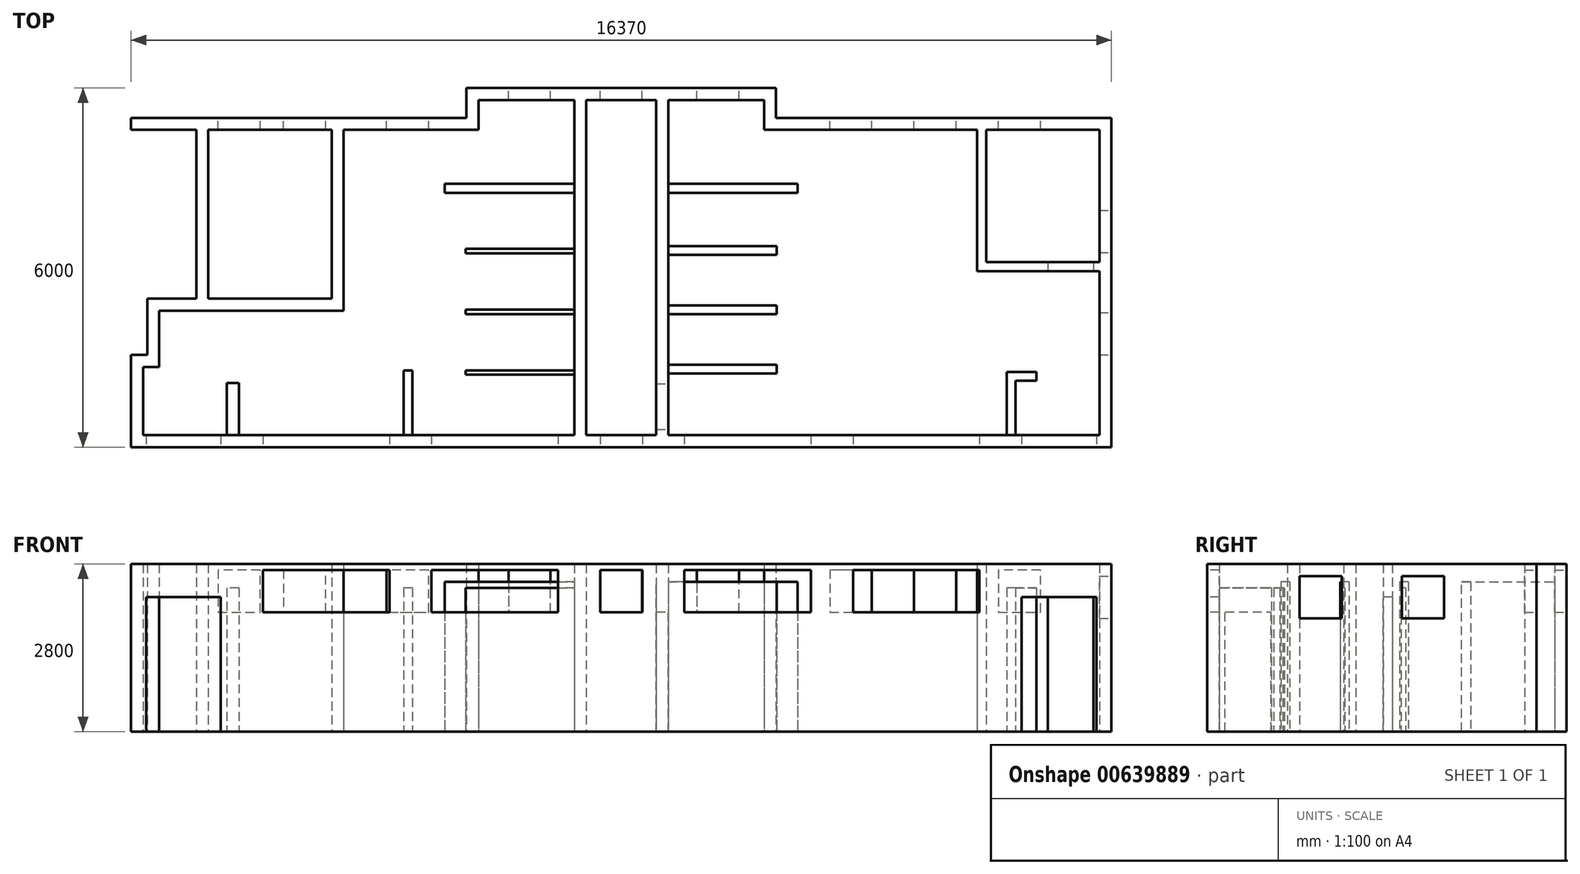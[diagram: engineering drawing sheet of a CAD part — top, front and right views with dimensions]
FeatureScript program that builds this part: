
annotation { "Feature Type Name" : "Feature", "Feature Type Description" : "" }
export const myFeature = defineFeature(function(context is Context, id is Id, definition is map)
    precondition{}
    {
        {
            var Q0;
            Q0=qCreatedBy(makeId("Top.planeOp"),FACE);
            var sketch = newSketch(context, id + "F0", { "sketchPlane" : qUnion([Q0])});
            skLineSegment(sketch, "E0", {"start": v(5800, 5300) * mm, "end": v(5800, 5800) * mm});
            skLineSegment(sketch, "E1", {"start": v(0, 0) * mm, "end": v(16370, 0) * mm});
            skLineSegment(sketch, "E2", {"start": v(16370, 0) * mm, "end": v(16370, 5500) * mm});
            skLineSegment(sketch, "E3", {"start": v(16370, 5500) * mm, "end": v(10770, 5500) * mm});
            skLineSegment(sketch, "E4", {"start": v(10770, 5500) * mm, "end": v(10770, 6000) * mm});
            skLineSegment(sketch, "E5", {"start": v(10770, 6000) * mm, "end": v(5600, 6000) * mm});
            skLineSegment(sketch, "E6", {"start": v(5600, 6000) * mm, "end": v(5600, 5500) * mm});
            skLineSegment(sketch, "E7", {"start": v(10570, 5800) * mm, "end": v(10570, 5300) * mm});
            skLineSegment(sketch, "E8", {"start": v(10570, 5300) * mm, "end": v(16170, 5300) * mm});
            skLineSegment(sketch, "E9", {"start": v(16170, 5300) * mm, "end": v(16170, 200) * mm});
            skLineSegment(sketch, "E10", {"start": v(0, 200) * mm, "end": v(0, 0) * mm});
            skLineSegment(sketch, "E11", {"start": v(0, 0) * mm, "end": v(0, 1540) * mm});
            skPoint(sketch, "E11.endSnap0", {"position": v(0, 100) * mm});
            skLineSegment(sketch, "E12", {"start": v(16170, 200) * mm, "end": v(200, 200) * mm});
            skLineSegment(sketch, "E13", {"start": v(200, 200) * mm, "end": v(200, 1340) * mm});
            skLineSegment(sketch, "E14", {"start": v(200, 1340) * mm, "end": v(470, 1340) * mm});
            skLineSegment(sketch, "E15", {"start": v(0, 1540) * mm, "end": v(270, 1540) * mm});
            skLineSegment(sketch, "E16", {"start": v(270, 1540) * mm, "end": v(270, 2480) * mm});
            skLineSegment(sketch, "E17", {"start": v(470, 1340) * mm, "end": v(470, 2280) * mm});
            skLineSegment(sketch, "E18", {"start": v(470, 2280) * mm, "end": v(936.4, 2280) * mm});
            skLineSegment(sketch, "E19", {"start": v(270, 2480) * mm, "end": v(1090, 2480) * mm});
            skLineSegment(sketch, "E20", {"start": v(5600, 5500) * mm, "end": v(1090, 5500) * mm});
            skLineSegment(sketch, "E21", {"start": v(5800, 5300) * mm, "end": v(1290, 5300) * mm});
            skLineSegment(sketch, "E22", {"start": v(1290, 5300) * mm, "end": v(1290, 2280) * mm});
            skLineSegment(sketch, "E23", {"start": v(1290, 2280) * mm, "end": v(936.4, 2280) * mm});
            skLineSegment(sketch, "E24", {"start": v(1090, 2480) * mm, "end": v(1090, 5500) * mm});
            skLineSegment(sketch, "E25", {"start": v(10570, 5800) * mm, "end": v(5800, 5800) * mm});
            skLineSegment(sketch, "E26", {"start": v(1090, 5500) * mm, "end": v(1090, 5300) * mm});
            skLineSegment(sketch, "E27", {"start": v(1090, 5500) * mm, "end": v(0, 5500) * mm});
            skLineSegment(sketch, "E28", {"start": v(0, 5500) * mm, "end": v(0, 5042) * mm});
            skLineSegment(sketch, "E29", {"start": v(0, 5042) * mm, "end": v(458, 5042) * mm});
            skLineSegment(sketch, "E30", {"start": v(458, 5042) * mm, "end": v(458, 5300) * mm});
            skLineSegment(sketch, "E31", {"start": v(458, 5300) * mm, "end": v(1090, 5300) * mm});
            skSolve(sketch);
        }
        {
            var Q0;
            {var subQ2=sQuery(id+"F0.wireOp",EDGE,"E1");Q0=makeQuery(id+"F0.imprint","IMPRINT",FACE,{"disambiguationData":[TD([[makeQuery(id+"F0.imprint","IMPRINT",EDGE,{"derivedFrom":subQ2}),1.0]])]});}
            extrude(context, id + "F1", {"entities" : qUnion([Q0]), "depth" : 2800 * mm, "offsetDistance" : 25 * mm});
        }
        {
            var Q0;
            Q0=makeQuery(id+"F1.opExtrude","SWEPT_FACE",FACE,{"disambiguationData":[OSD([sQuery(id+"F0.wireOp",EDGE,"E1")])]});
            var sketch = newSketch(context, id + "F2", { "sketchPlane" : qUnion([Q0])});
            skLineSegment(sketch, "E32", {"start": v(250, 0) * mm, "end": v(250, 2250) * mm});
            skLineSegment(sketch, "E33", {"start": v(250, 2250) * mm, "end": v(1500, 2250) * mm});
            skLineSegment(sketch, "E34", {"start": v(1500, 2250) * mm, "end": v(1500, 0) * mm});
            skLineSegment(sketch, "E35", {"start": v(1500, 0) * mm, "end": v(250, 0) * mm});
            skSolve(sketch);
        }
        {
            var Q0;
            Q0=makeQuery(id+"F2.imprint","IMPRINT",FACE,{"disambiguationData":[TD([[makeQuery(id+"F2.imprint","IMPRINT",EDGE,{"derivedFrom":sQuery(id+"F2.wireOp",EDGE,"E32")}),-1.0]])]});
            extrude(context, id + "F3", {"entities" : qUnion([Q0]), "operationType" : NewBodyOperationType.REMOVE, "oppositeDirection" : true, "depth" : 200 * mm, "offsetDistance" : 25 * mm});
        }
        {
            var Q0;
            Q0=makeQuery(id+"F1.opExtrude","SWEPT_FACE",FACE,{"disambiguationData":[OSD([sQuery(id+"F0.wireOp",EDGE,"E1")])]});
            var sketch = newSketch(context, id + "F4", { "sketchPlane" : qUnion([Q0])});
            skLineSegment(sketch, "E36", {"start": v(16120, 0) * mm, "end": v(16120, 2250) * mm});
            skLineSegment(sketch, "E37", {"start": v(16120, 2250) * mm, "end": v(14870, 2250) * mm});
            skLineSegment(sketch, "E38", {"start": v(14870, 2250) * mm, "end": v(14870, 0) * mm});
            skLineSegment(sketch, "E39", {"start": v(14870, 0) * mm, "end": v(16120, 0) * mm});
            skSolve(sketch);
        }
        {
            var Q0;
            Q0=makeQuery(id+"F4.imprint","IMPRINT",FACE,{"disambiguationData":[TD([[makeQuery(id+"F4.imprint","IMPRINT",EDGE,{"derivedFrom":sQuery(id+"F4.wireOp",EDGE,"E36")}),1.0]])]});
            extrude(context, id + "F5", {"entities" : qUnion([Q0]), "operationType" : NewBodyOperationType.REMOVE, "oppositeDirection" : true, "depth" : 200 * mm, "offsetDistance" : 25 * mm});
        }
        {
            var Q0;
            Q0=qCreatedBy(makeId("Top.planeOp"),FACE);
            var sketch = newSketch(context, id + "F6", { "sketchPlane" : qUnion([Q0])});
            skLineSegment(sketch, "E40", {"start": v(1290, 2280) * mm, "end": v(3550, 2280) * mm});
            skLineSegment(sketch, "E41", {"start": v(3550, 2280) * mm, "end": v(3550, 5300) * mm});
            skLineSegment(sketch, "E42", {"start": v(3550, 5300) * mm, "end": v(3350, 5300) * mm});
            skLineSegment(sketch, "E43", {"start": v(3350, 2480) * mm, "end": v(1290, 2480) * mm});
            skLineSegment(sketch, "E44", {"start": v(1290, 2480) * mm, "end": v(1290, 2280) * mm});
            skLineSegment(sketch, "E45", {"start": v(3350, 5300) * mm, "end": v(3350, 2480) * mm});
            skSolve(sketch);
        }
        {
            var Q0;
            Q0=makeQuery(id+"F6.imprint","IMPRINT",FACE,{"disambiguationData":[TD([[makeQuery(id+"F6.imprint","IMPRINT",EDGE,{"derivedFrom":sQuery(id+"F6.wireOp",EDGE,"E40")}),1.0]])]});
            extrude(context, id + "F7", {"entities" : qUnion([Q0]), "operationType" : NewBodyOperationType.ADD, "depth" : 2800 * mm, "offsetDistance" : 25 * mm});
        }
        {
            var Q0;
            Q0=qCreatedBy(makeId("Top.planeOp"),FACE);
            var sketch = newSketch(context, id + "F8", { "sketchPlane" : qUnion([Q0])});
            skLineSegment(sketch, "E46.0", {"start": v(5800, 5300) * mm, "end": v(5800, 5800) * mm});
            skLineSegment(sketch, "E47.0", {"start": v(10570, 5800) * mm, "end": v(5800, 5800) * mm});
            skLineSegment(sketch, "E48.0", {"start": v(16170, 200) * mm, "end": v(200, 200) * mm});
            skLineSegment(sketch, "E49", {"start": v(5800, 5800) * mm, "end": v(7400, 5800) * mm});
            skLineSegment(sketch, "E50", {"start": v(7400, 5800) * mm, "end": v(7600, 5800) * mm});
            skLineSegment(sketch, "E51", {"start": v(7600, 5800) * mm, "end": v(7600, 200) * mm});
            skLineSegment(sketch, "E52", {"start": v(7400, 5800) * mm, "end": v(7400, 200) * mm});
            skSolve(sketch);
        }
        {
            var Q0;
            Q0=qCreatedBy(makeId("Top.planeOp"),FACE);
            var sketch = newSketch(context, id + "F9", { "sketchPlane" : qUnion([Q0])});
            skLineSegment(sketch, "E53.0", {"start": v(10570, 5800) * mm, "end": v(10570, 5300) * mm});
            skLineSegment(sketch, "E53.1", {"start": v(10570, 5800) * mm, "end": v(5800, 5800) * mm});
            skLineSegment(sketch, "E53.2", {"start": v(16170, 200) * mm, "end": v(200, 200) * mm});
            skLineSegment(sketch, "E54", {"start": v(8970, 200) * mm, "end": v(8770, 200) * mm});
            skLineSegment(sketch, "E55", {"start": v(8770, 200) * mm, "end": v(8770, 5800) * mm});
            skLineSegment(sketch, "E56", {"start": v(8770, 5800) * mm, "end": v(8970, 5800) * mm});
            skLineSegment(sketch, "E57", {"start": v(8970, 5800) * mm, "end": v(8970, 200) * mm});
            skSolve(sketch);
        }
        {
            var Q0;
            Q0=qSketchRegion(id+"F8",true);
            extrude(context, id + "F10", {"entities" : qUnion([Q0]), "operationType" : NewBodyOperationType.ADD, "depth" : 2800 * mm, "offsetDistance" : 25 * mm});
        }
        {
            var Q0;
            Q0=qSketchRegion(id+"F9",true);
            extrude(context, id + "F11", {"entities" : qUnion([Q0]), "operationType" : NewBodyOperationType.ADD, "depth" : 2800 * mm, "offsetDistance" : 25 * mm});
        }
        {
            var Q0;
            Q0=qCreatedBy(makeId("Top.planeOp"),FACE);
            var sketch = newSketch(context, id + "F12", { "sketchPlane" : qUnion([Q0])});
            skLineSegment(sketch, "E58.0", {"start": v(10570, 5800) * mm, "end": v(5800, 5800) * mm});
            skLineSegment(sketch, "E58.1", {"start": v(10570, 5800) * mm, "end": v(10570, 5300) * mm});
            skLineSegment(sketch, "E59", {"start": v(10570, 5800) * mm, "end": v(8969, 5800) * mm});
            skLineSegment(sketch, "E60", {"start": v(8969, 5800) * mm, "end": v(8969, 4400) * mm});
            skLineSegment(sketch, "E61", {"start": v(8969, 4400) * mm, "end": v(11129, 4400) * mm});
            skLineSegment(sketch, "E62", {"start": v(11129, 4400) * mm, "end": v(11129, 4250) * mm});
            skLineSegment(sketch, "E63", {"start": v(11129, 4250) * mm, "end": v(8769, 4250) * mm});
            skLineSegment(sketch, "E64", {"start": v(8769, 4250) * mm, "end": v(8769, 5800) * mm});
            skSolve(sketch);
        }
        {
            var Q0;
            Q0=qCreatedBy(makeId("Top.planeOp"),FACE);
            var sketch = newSketch(context, id + "F13", { "sketchPlane" : qUnion([Q0])});
            skLineSegment(sketch, "E65", {"start": v(7400, 5800) * mm, "end": v(7400, 4400) * mm});
            skLineSegment(sketch, "E66", {"start": v(7400, 4400) * mm, "end": v(5240, 4400) * mm});
            skLineSegment(sketch, "E67", {"start": v(5240, 4400) * mm, "end": v(5240, 4250) * mm});
            skLineSegment(sketch, "E68", {"start": v(5240, 4250) * mm, "end": v(7600, 4250) * mm});
            skLineSegment(sketch, "E69", {"start": v(7600, 4250) * mm, "end": v(7600, 5800) * mm});
            skLineSegment(sketch, "E70", {"start": v(7400, 5800) * mm, "end": v(7600, 5800) * mm});
            skSolve(sketch);
        }
        {
            var Q0;
            Q0=qSketchRegion(id+"F13",true);
            extrude(context, id + "F14", {"entities" : qUnion([Q0]), "operationType" : NewBodyOperationType.ADD, "depth" : 2500 * mm, "offsetDistance" : 25 * mm});
        }
        {
            var Q0;
            Q0=qCreatedBy(makeId("Top.planeOp"),FACE);
            var sketch = newSketch(context, id + "F15", { "sketchPlane" : qUnion([Q0])});
            skLineSegment(sketch, "E71.0", {"start": v(10570, 5300) * mm, "end": v(16170, 5300) * mm});
            skLineSegment(sketch, "E71.1", {"start": v(16170, 5300) * mm, "end": v(16170, 200) * mm});
            skLineSegment(sketch, "E72", {"start": v(16170, 5300) * mm, "end": v(16170, 3090) * mm});
            skLineSegment(sketch, "E73", {"start": v(16170, 3090) * mm, "end": v(14280, 3090) * mm});
            skLineSegment(sketch, "E74", {"start": v(14280, 3090) * mm, "end": v(14280, 5300) * mm});
            skLineSegment(sketch, "E75", {"start": v(14280, 5300) * mm, "end": v(14130, 5300) * mm});
            skLineSegment(sketch, "E76", {"start": v(14130, 5300) * mm, "end": v(14130, 2940) * mm});
            skLineSegment(sketch, "E77", {"start": v(14130, 2940) * mm, "end": v(16170, 2940) * mm});
            skSolve(sketch);
        }
        {
            var Q0;
            {var subQ0=sQuery(id+"F15.wireOp",EDGE,"E73");Q0=makeQuery(id+"F15.imprint","IMPRINT",FACE,{"disambiguationData":[TD([[makeQuery(id+"F15.imprint","IMPRINT",EDGE,{"derivedFrom":subQ0}),1.0]])]});}
            extrude(context, id + "F16", {"entities" : qUnion([Q0]), "operationType" : NewBodyOperationType.ADD, "depth" : 2800 * mm, "offsetDistance" : 25 * mm});
        }
        {
            var Q0;
            Q0=makeQuery(id+"F1.opExtrude","SWEPT_FACE",FACE,{"disambiguationData":[OSD([sQuery(id+"F0.wireOp",EDGE,"E1")])]});
            var sketch = newSketch(context, id + "F17", { "sketchPlane" : qUnion([Q0])});
            skLineSegment(sketch, "E78", {"start": v(2204, 1996) * mm, "end": v(2204, 2700) * mm});
            skLineSegment(sketch, "E79", {"start": v(2204, 2700) * mm, "end": v(4315, 2700) * mm});
            skLineSegment(sketch, "E80", {"start": v(4315, 2700) * mm, "end": v(4315, 1996) * mm});
            skLineSegment(sketch, "E81", {"start": v(4315, 1996) * mm, "end": v(2204, 1996) * mm});
            skLineSegment(sketch, "E82", {"start": v(5018, 1996) * mm, "end": v(5018, 2700) * mm});
            skLineSegment(sketch, "E83", {"start": v(5018, 2700) * mm, "end": v(7129, 2700) * mm});
            skLineSegment(sketch, "E84", {"start": v(7129, 2700) * mm, "end": v(7129, 1996) * mm});
            skLineSegment(sketch, "E85", {"start": v(7129, 1996) * mm, "end": v(5018, 1996) * mm});
            skLineSegment(sketch, "E86", {"start": v(7833, 1996) * mm, "end": v(7833, 2700) * mm});
            skLineSegment(sketch, "E87", {"start": v(7833, 2700) * mm, "end": v(8537, 2700) * mm});
            skLineSegment(sketch, "E88", {"start": v(8537, 2700) * mm, "end": v(8537, 1996) * mm});
            skLineSegment(sketch, "E89", {"start": v(8537, 1996) * mm, "end": v(7833, 1996) * mm});
            skLineSegment(sketch, "E90", {"start": v(9241, 1996) * mm, "end": v(9241, 2700) * mm});
            skLineSegment(sketch, "E91", {"start": v(9241, 2700) * mm, "end": v(11352, 2700) * mm});
            skLineSegment(sketch, "E92", {"start": v(11352, 2700) * mm, "end": v(11352, 1996) * mm});
            skLineSegment(sketch, "E93", {"start": v(11352, 1996) * mm, "end": v(9241, 1996) * mm});
            skLineSegment(sketch, "E94", {"start": v(12056, 1996) * mm, "end": v(12056, 2700) * mm});
            skLineSegment(sketch, "E95", {"start": v(12056, 2700) * mm, "end": v(14167, 2700) * mm});
            skLineSegment(sketch, "E96", {"start": v(14167, 2700) * mm, "end": v(14167, 1996) * mm});
            skLineSegment(sketch, "E97", {"start": v(14167, 1996) * mm, "end": v(12056, 1996) * mm});
            skSolve(sketch);
        }
        {
            var Q0;
            Q0=makeQuery(id+"F17.imprint","IMPRINT",FACE,{"disambiguationData":[TD([[makeQuery(id+"F17.imprint","IMPRINT",EDGE,{"derivedFrom":sQuery(id+"F17.wireOp",EDGE,"E78")}),-1.0]])]});
            var Q1;
            Q1=makeQuery(id+"F17.imprint","IMPRINT",FACE,{"disambiguationData":[TD([[makeQuery(id+"F17.imprint","IMPRINT",EDGE,{"derivedFrom":sQuery(id+"F17.wireOp",EDGE,"E82")}),-1.0]])]});
            var Q2;
            Q2=makeQuery(id+"F17.imprint","IMPRINT",FACE,{"disambiguationData":[TD([[makeQuery(id+"F17.imprint","IMPRINT",EDGE,{"derivedFrom":sQuery(id+"F17.wireOp",EDGE,"E86")}),-1.0]])]});
            var Q3;
            Q3=makeQuery(id+"F17.imprint","IMPRINT",FACE,{"disambiguationData":[TD([[makeQuery(id+"F17.imprint","IMPRINT",EDGE,{"derivedFrom":sQuery(id+"F17.wireOp",EDGE,"E90")}),-1.0]])]});
            var Q4;
            Q4=makeQuery(id+"F17.imprint","IMPRINT",FACE,{"disambiguationData":[TD([[makeQuery(id+"F17.imprint","IMPRINT",EDGE,{"derivedFrom":sQuery(id+"F17.wireOp",EDGE,"E94")}),-1.0]])]});
            extrude(context, id + "F18", {"entities" : qUnion([Q0, Q1, Q2, Q3, Q4]), "operationType" : NewBodyOperationType.REMOVE, "oppositeDirection" : true, "depth" : 200 * mm, "offsetDistance" : 25 * mm});
        }
        {
            var Q0;
            {var subQ0=sQuery(id+"F12.wireOp",EDGE,"E60");Q0=makeQuery(id+"F12.imprint","IMPRINT",FACE,{"disambiguationData":[TD([[makeQuery(id+"F12.imprint","IMPRINT",EDGE,{"derivedFrom":subQ0}),-1.0]])]});}
            extrude(context, id + "F19", {"entities" : qUnion([Q0]), "operationType" : NewBodyOperationType.ADD, "depth" : 2500 * mm, "offsetDistance" : 25 * mm});
        }
        {
            var Q0;
            Q0=makeQuery(id+"F1.opExtrude","SWEPT_FACE",FACE,{"disambiguationData":[OSD([sQuery(id+"F0.wireOp",EDGE,"E3")])]});
            var sketch = newSketch(context, id + "F20", { "sketchPlane" : qUnion([Q0])});
            skLineSegment(sketch, "E98", {"start": v(-15187, 1996) * mm, "end": v(-15187, 2700) * mm});
            skLineSegment(sketch, "E99", {"start": v(-15187, 2700) * mm, "end": v(-14483, 2700) * mm});
            skLineSegment(sketch, "E100", {"start": v(-14483, 2700) * mm, "end": v(-14483, 1996) * mm});
            skLineSegment(sketch, "E101", {"start": v(-14483, 1996) * mm, "end": v(-15187, 1996) * mm});
            skLineSegment(sketch, "E102", {"start": v(-13779, 1996) * mm, "end": v(-13779, 2700) * mm});
            skLineSegment(sketch, "E103", {"start": v(-13779, 2700) * mm, "end": v(-13075, 2700) * mm});
            skLineSegment(sketch, "E104", {"start": v(-13075, 2700) * mm, "end": v(-13075, 1996) * mm});
            skLineSegment(sketch, "E105", {"start": v(-13075, 1996) * mm, "end": v(-13779, 1996) * mm});
            skLineSegment(sketch, "E106", {"start": v(-12371, 1996) * mm, "end": v(-12371, 2700) * mm});
            skLineSegment(sketch, "E107", {"start": v(-12371, 2700) * mm, "end": v(-11667, 2700) * mm});
            skLineSegment(sketch, "E108", {"start": v(-11667, 2700) * mm, "end": v(-11667, 1996) * mm});
            skLineSegment(sketch, "E109", {"start": v(-11667, 1996) * mm, "end": v(-12371, 1996) * mm});
            skSolve(sketch);
        }
        {
            var Q0;
            Q0=makeQuery(id+"F20.imprint","IMPRINT",FACE,{"disambiguationData":[TD([[makeQuery(id+"F20.imprint","IMPRINT",EDGE,{"derivedFrom":sQuery(id+"F20.wireOp",EDGE,"E98")}),-1.0]])]});
            var Q1;
            Q1=makeQuery(id+"F20.imprint","IMPRINT",FACE,{"disambiguationData":[TD([[makeQuery(id+"F20.imprint","IMPRINT",EDGE,{"derivedFrom":sQuery(id+"F20.wireOp",EDGE,"E102")}),-1.0]])]});
            var Q2;
            Q2=makeQuery(id+"F20.imprint","IMPRINT",FACE,{"disambiguationData":[TD([[makeQuery(id+"F20.imprint","IMPRINT",EDGE,{"derivedFrom":sQuery(id+"F20.wireOp",EDGE,"E106")}),-1.0]])]});
            extrude(context, id + "F21", {"entities" : qUnion([Q0, Q1, Q2]), "operationType" : NewBodyOperationType.REMOVE, "oppositeDirection" : true, "depth" : 200 * mm, "offsetDistance" : 25 * mm});
        }
        {
            var Q0;
            Q0=makeQuery(id+"F1.opExtrude","SWEPT_FACE",FACE,{"disambiguationData":[OSD([sQuery(id+"F0.wireOp",EDGE,"E5")])]});
            var sketch = newSketch(context, id + "F22", { "sketchPlane" : qUnion([Q0])});
            skLineSegment(sketch, "E110", {"start": v(-10150, 1996) * mm, "end": v(-10150, 2700) * mm});
            skLineSegment(sketch, "E111", {"start": v(-10150, 2700) * mm, "end": v(-9446, 2700) * mm});
            skLineSegment(sketch, "E112", {"start": v(-9446, 2700) * mm, "end": v(-9446, 1996) * mm});
            skLineSegment(sketch, "E113", {"start": v(-9446, 1996) * mm, "end": v(-10150, 1996) * mm});
            skLineSegment(sketch, "E114", {"start": v(-8536, 1996) * mm, "end": v(-8536, 2700) * mm});
            skLineSegment(sketch, "E115", {"start": v(-8536, 2700) * mm, "end": v(-7832, 2700) * mm});
            skLineSegment(sketch, "E116", {"start": v(-7832, 2700) * mm, "end": v(-7832, 1996) * mm});
            skLineSegment(sketch, "E117", {"start": v(-7832, 1996) * mm, "end": v(-8536, 1996) * mm});
            skLineSegment(sketch, "E118", {"start": v(-7005, 1996) * mm, "end": v(-7005, 2700) * mm});
            skLineSegment(sketch, "E119", {"start": v(-7005, 2700) * mm, "end": v(-6301, 2700) * mm});
            skLineSegment(sketch, "E120", {"start": v(-6301, 2700) * mm, "end": v(-6301, 1996) * mm});
            skLineSegment(sketch, "E121", {"start": v(-6301, 1996) * mm, "end": v(-7005, 1996) * mm});
            skSolve(sketch);
        }
        {
            var Q0;
            Q0=makeQuery(id+"F22.imprint","IMPRINT",FACE,{"disambiguationData":[TD([[makeQuery(id+"F22.imprint","IMPRINT",EDGE,{"derivedFrom":sQuery(id+"F22.wireOp",EDGE,"E110")}),-1.0]])]});
            var Q1;
            Q1=makeQuery(id+"F22.imprint","IMPRINT",FACE,{"disambiguationData":[TD([[makeQuery(id+"F22.imprint","IMPRINT",EDGE,{"derivedFrom":sQuery(id+"F22.wireOp",EDGE,"E114")}),-1.0]])]});
            var Q2;
            Q2=makeQuery(id+"F22.imprint","IMPRINT",FACE,{"disambiguationData":[TD([[makeQuery(id+"F22.imprint","IMPRINT",EDGE,{"derivedFrom":sQuery(id+"F22.wireOp",EDGE,"E118")}),-1.0]])]});
            extrude(context, id + "F23", {"entities" : qUnion([Q0, Q1, Q2]), "operationType" : NewBodyOperationType.REMOVE, "oppositeDirection" : true, "depth" : 200 * mm, "offsetDistance" : 25 * mm});
        }
        {
            var Q0;
            Q0=makeQuery(id+"F1.opExtrude","SWEPT_FACE",FACE,{"disambiguationData":[OSD([sQuery(id+"F0.wireOp",EDGE,"E20")])]});
            var sketch = newSketch(context, id + "F24", { "sketchPlane" : qUnion([Q0])});
            skLineSegment(sketch, "E122", {"start": v(-4969, 1996) * mm, "end": v(-4969, 2700) * mm});
            skLineSegment(sketch, "E123", {"start": v(-4969, 2700) * mm, "end": v(-4265, 2700) * mm});
            skLineSegment(sketch, "E124", {"start": v(-4265, 2700) * mm, "end": v(-4265, 1996) * mm});
            skLineSegment(sketch, "E125", {"start": v(-4265, 1996) * mm, "end": v(-4969, 1996) * mm});
            skLineSegment(sketch, "E126", {"start": v(-3248, 1996) * mm, "end": v(-3248, 2700) * mm});
            skLineSegment(sketch, "E127", {"start": v(-3248, 2700) * mm, "end": v(-2544, 2700) * mm});
            skLineSegment(sketch, "E128", {"start": v(-2544, 2700) * mm, "end": v(-2544, 1996) * mm});
            skLineSegment(sketch, "E129", {"start": v(-2544, 1996) * mm, "end": v(-3248, 1996) * mm});
            skLineSegment(sketch, "E130", {"start": v(-2156, 1996) * mm, "end": v(-2156, 2700) * mm});
            skLineSegment(sketch, "E131", {"start": v(-2156, 2700) * mm, "end": v(-1452, 2700) * mm});
            skLineSegment(sketch, "E132", {"start": v(-1452, 2700) * mm, "end": v(-1452, 1996) * mm});
            skLineSegment(sketch, "E133", {"start": v(-1452, 1996) * mm, "end": v(-2156, 1996) * mm});
            skSolve(sketch);
        }
        {
            var Q0;
            Q0=makeQuery(id+"F24.imprint","IMPRINT",FACE,{"disambiguationData":[TD([[makeQuery(id+"F24.imprint","IMPRINT",EDGE,{"derivedFrom":sQuery(id+"F24.wireOp",EDGE,"E122")}),-1.0]])]});
            var Q1;
            Q1=makeQuery(id+"F24.imprint","IMPRINT",FACE,{"disambiguationData":[TD([[makeQuery(id+"F24.imprint","IMPRINT",EDGE,{"derivedFrom":sQuery(id+"F24.wireOp",EDGE,"E126")}),-1.0]])]});
            var Q2;
            Q2=makeQuery(id+"F24.imprint","IMPRINT",FACE,{"disambiguationData":[TD([[makeQuery(id+"F24.imprint","IMPRINT",EDGE,{"derivedFrom":sQuery(id+"F24.wireOp",EDGE,"E130")}),-1.0]])]});
            extrude(context, id + "F25", {"entities" : qUnion([Q0, Q1, Q2]), "operationType" : NewBodyOperationType.REMOVE, "oppositeDirection" : true, "depth" : 200 * mm, "offsetDistance" : 25 * mm});
        }
        {
            var Q0;
            Q0=makeQuery(id+"F10.opExtrude","SWEPT_FACE",FACE,{"disambiguationData":[OSD([sQuery(id+"F8.wireOp",EDGE,"E51")])]});
            var sketch = newSketch(context, id + "F26", { "sketchPlane" : qUnion([Q0])});
            skLineSegment(sketch, "E134.0", {"start": v(5800, 2800) * mm, "end": v(5800, 0) * mm});
            skLineSegment(sketch, "E135.0", {"start": v(4250, 0) * mm, "end": v(5800, 0) * mm});
            skLineSegment(sketch, "E136", {"start": v(5800, 0) * mm, "end": v(2800, 0) * mm});
            skLineSegment(sketch, "E137", {"start": v(2800, 0) * mm, "end": v(2800, 2100) * mm});
            skLineSegment(sketch, "E138", {"start": v(2800, 2100) * mm, "end": v(1200, 2100) * mm});
            skLineSegment(sketch, "E139", {"start": v(1200, 2100) * mm, "end": v(1200, 0) * mm});
            skLineSegment(sketch, "E140", {"start": v(1200, 0) * mm, "end": v(2800, 0) * mm});
            skSolve(sketch);
        }
        {
            var Q0;
            {var subQ0=sQuery(id+"F13.wireOp",EDGE,"E66");Q0=makeQuery(id+"FqNkP1vWDE5f3xF_1.boolean.opBoolean","MERGE",FACE,{"derivedFrom":[makeQuery(id+"F14.opExtrude","SWEPT_FACE",FACE,{"disambiguationData":[OSD([subQ0])]}),makeQuery(id+"FqNkP1vWDE5f3xF_1.opExtrude","SWEPT_FACE",FACE,{"disambiguationData":[OSD([subQ0])]})]});}
            var sketch = newSketch(context, id + "F27", { "sketchPlane" : qUnion([Q0])});
            skLineSegment(sketch, "E141", {"start": v(-5240, 2800) * mm, "end": v(-5240, 2450) * mm});
            skLineSegment(sketch, "E142", {"start": v(-5240, 2450) * mm, "end": v(-5390, 2450) * mm});
            skLineSegment(sketch, "E143", {"start": v(-5390, 2450) * mm, "end": v(-5390, 2800) * mm});
            skLineSegment(sketch, "E144", {"start": v(-5390, 2800) * mm, "end": v(-5240, 2800) * mm});
            skSolve(sketch);
        }
        {
            var Q0;
            Q0=makeQuery(id+"F16.opExtrude","SWEPT_FACE",FACE,{"disambiguationData":[OSD([sQuery(id+"F15.wireOp",EDGE,"E77")])]});
            var sketch = newSketch(context, id + "F28", { "sketchPlane" : qUnion([Q0])});
            skLineSegment(sketch, "E145.0", {"start": v(16170, 2800) * mm, "end": v(16170, 0) * mm});
            skLineSegment(sketch, "E146", {"start": v(16170, 0) * mm, "end": v(16070, 0) * mm});
            skLineSegment(sketch, "E147", {"start": v(16070, 0) * mm, "end": v(16070, 2250) * mm});
            skLineSegment(sketch, "E148", {"start": v(16070, 2250) * mm, "end": v(15310, 2250) * mm});
            skLineSegment(sketch, "E149", {"start": v(15310, 2250) * mm, "end": v(15310, 0) * mm});
            skLineSegment(sketch, "E150", {"start": v(15310, 0) * mm, "end": v(16070, 0) * mm});
            skSolve(sketch);
        }
        {
            var Q0;
            Q0=qSketchRegion(id+"F28",true);
            extrude(context, id + "F29", {"entities" : qUnion([Q0]), "operationType" : NewBodyOperationType.REMOVE, "oppositeDirection" : true, "depth" : 150 * mm, "offsetDistance" : 25 * mm});
        }
        {
            var Q0;
            Q0=makeQuery(id+"F1.opExtrude","SWEPT_FACE",FACE,{"disambiguationData":[OSD([sQuery(id+"F0.wireOp",EDGE,"E2")])]});
            var sketch = newSketch(context, id + "F30", { "sketchPlane" : qUnion([Q0])});
            skLineSegment(sketch, "E151.0", {"start": v(0, 2800) * mm, "end": v(0, 0) * mm});
            skLineSegment(sketch, "E152", {"start": v(1545, 2600) * mm, "end": v(1545, 1895) * mm});
            skLineSegment(sketch, "E153", {"start": v(1545, 1895) * mm, "end": v(2250, 1895) * mm});
            skLineSegment(sketch, "E154", {"start": v(2250, 1895) * mm, "end": v(2250, 2600) * mm});
            skLineSegment(sketch, "E155", {"start": v(2250, 2600) * mm, "end": v(1545, 2600) * mm});
            skLineSegment(sketch, "E156", {"start": v(3250, 2600) * mm, "end": v(3250, 1895) * mm});
            skLineSegment(sketch, "E157", {"start": v(3250, 1895) * mm, "end": v(3955, 1895) * mm});
            skLineSegment(sketch, "E158", {"start": v(3955, 1895) * mm, "end": v(3955, 2600) * mm});
            skLineSegment(sketch, "E159", {"start": v(3955, 2600) * mm, "end": v(3250, 2600) * mm});
            skSolve(sketch);
        }
        {
            var Q0;
            Q0=makeQuery(id+"F30.imprint","IMPRINT",FACE,{"disambiguationData":[TD([[makeQuery(id+"F30.imprint","IMPRINT",EDGE,{"derivedFrom":sQuery(id+"F30.wireOp",EDGE,"E152")}),1.0]])]});
            var Q1;
            Q1=makeQuery(id+"F30.imprint","IMPRINT",FACE,{"disambiguationData":[TD([[makeQuery(id+"F30.imprint","IMPRINT",EDGE,{"derivedFrom":sQuery(id+"F30.wireOp",EDGE,"E156")}),1.0]])]});
            extrude(context, id + "F31", {"entities" : qUnion([Q0, Q1]), "operationType" : NewBodyOperationType.REMOVE, "oppositeDirection" : true, "depth" : 200 * mm, "offsetDistance" : 25 * mm});
        }
        {
            var Q0;
            Q0=qCreatedBy(makeId("Top.planeOp"),FACE);
            var sketch = newSketch(context, id + "F32", { "sketchPlane" : qUnion([Q0])});
            skLineSegment(sketch, "E160.0", {"start": v(10570, 5800) * mm, "end": v(8969, 5800) * mm});
            skLineSegment(sketch, "E161.0", {"start": v(8970, 5800) * mm, "end": v(8970, 200) * mm});
            skLineSegment(sketch, "E162", {"start": v(8970, 5800) * mm, "end": v(8970, 3360) * mm});
            skLineSegment(sketch, "E163", {"start": v(8970, 3360) * mm, "end": v(10780, 3360) * mm});
            skLineSegment(sketch, "E164", {"start": v(10780, 3360) * mm, "end": v(10780, 3210) * mm});
            skLineSegment(sketch, "E165", {"start": v(10780, 3210) * mm, "end": v(8970, 3210) * mm});
            skLineSegment(sketch, "E166", {"start": v(8970, 3210) * mm, "end": v(8970, 2370) * mm});
            skLineSegment(sketch, "E167", {"start": v(8970, 2370) * mm, "end": v(10780, 2370) * mm});
            skLineSegment(sketch, "E168", {"start": v(10780, 2370) * mm, "end": v(10780, 2220) * mm});
            skLineSegment(sketch, "E169", {"start": v(10780, 2220) * mm, "end": v(8970, 2220) * mm});
            skLineSegment(sketch, "E170", {"start": v(8970, 2220) * mm, "end": v(8970, 1380) * mm});
            skLineSegment(sketch, "E171", {"start": v(8970, 1380) * mm, "end": v(10780, 1380) * mm});
            skLineSegment(sketch, "E172", {"start": v(10780, 1380) * mm, "end": v(10780, 1230) * mm});
            skLineSegment(sketch, "E173", {"start": v(10780, 1230) * mm, "end": v(8970, 1230) * mm});
            skLineSegment(sketch, "E174", {"start": v(8970, 1230) * mm, "end": v(8770, 1230) * mm});
            skLineSegment(sketch, "E175", {"start": v(8770, 1230) * mm, "end": v(8770, 5800) * mm});
            skLineSegment(sketch, "E176", {"start": v(8770, 5800) * mm, "end": v(8970, 5800) * mm});
            skSolve(sketch);
        }
        {
            var Q0;
            Q0=qSketchRegion(id+"F32",true);
            extrude(context, id + "F33", {"entities" : qUnion([Q0]), "operationType" : NewBodyOperationType.ADD, "depth" : 2500 * mm, "offsetDistance" : 25 * mm});
        }
        {
            var Q0;
            Q0=makeQuery(id+"F11.opExtrude","SWEPT_FACE",FACE,{"disambiguationData":[OSD([sQuery(id+"F9.wireOp",EDGE,"E57")])]});
            var sketch = newSketch(context, id + "F34", { "sketchPlane" : qUnion([Q0])});
            skLineSegment(sketch, "E177.0", {"start": v(0, 2800) * mm, "end": v(0, 0) * mm});
            skLineSegment(sketch, "E178", {"start": v(200, 0) * mm, "end": v(962, 0) * mm});
            skLineSegment(sketch, "E179", {"start": v(0, 0) * mm, "end": v(300, 0) * mm});
            skLineSegment(sketch, "E180", {"start": v(300, 0) * mm, "end": v(300, 2000) * mm});
            skLineSegment(sketch, "E181", {"start": v(300, 2000) * mm, "end": v(1062, 2000) * mm});
            skLineSegment(sketch, "E182", {"start": v(1062, 2000) * mm, "end": v(1062, 0) * mm});
            skLineSegment(sketch, "E183", {"start": v(1062, 0) * mm, "end": v(300, 0) * mm});
            skSolve(sketch);
        }
        {
            var Q0;
            {var subQ0=sQuery(id+"F34.wireOp",EDGE,"E180");Q0=makeQuery(id+"F34.imprint","IMPRINT",FACE,{"disambiguationData":[TD([[makeQuery(id+"F34.imprint","IMPRINT",EDGE,{"derivedFrom":subQ0}),-1.0]])]});}
            extrude(context, id + "F35", {"entities" : qUnion([Q0]), "operationType" : NewBodyOperationType.REMOVE, "oppositeDirection" : true, "depth" : 200 * mm, "offsetDistance" : 25 * mm});
        }
        {
            var Q0;
            Q0=qCreatedBy(makeId("Top.planeOp"),FACE);
            var sketch = newSketch(context, id + "F36", { "sketchPlane" : qUnion([Q0])});
            skLineSegment(sketch, "E184.0", {"start": v(200, 200) * mm, "end": v(200, 1340) * mm});
            skLineSegment(sketch, "E184.1", {"start": v(7400, 200) * mm, "end": v(200, 200) * mm});
            skLineSegment(sketch, "E185", {"start": v(1600, 200) * mm, "end": v(1600, 1070) * mm});
            skLineSegment(sketch, "E186", {"start": v(1600, 1070) * mm, "end": v(1800, 1070) * mm});
            skLineSegment(sketch, "E187", {"start": v(1800, 1070) * mm, "end": v(1800, 200) * mm});
            skLineSegment(sketch, "E188", {"start": v(1800, 200) * mm, "end": v(1600, 200) * mm});
            skSolve(sketch);
        }
        {
            var Q0;
            Q0 = qSketchRegion(id + "F36", true);
            extrude(context, id + "F37", {"entities" : qUnion([Q0]), "operationType" : NewBodyOperationType.ADD, "depth" : 2400 * mm, "offsetDistance" : 25 * mm});
        }
        {
            var Q0;
            Q0=qCreatedBy(makeId("Top.planeOp"),FACE);
            var sketch = newSketch(context, id + "F38", { "sketchPlane" : qUnion([Q0])});
            skLineSegment(sketch, "E189.0", {"start": v(1800, 1070) * mm, "end": v(1800, 200) * mm});
            skLineSegment(sketch, "E189.1", {"start": v(7400, 200) * mm, "end": v(200, 200) * mm});
            skLineSegment(sketch, "E190", {"start": v(4550, 200) * mm, "end": v(4550, 1285) * mm});
            skLineSegment(sketch, "E191", {"start": v(4550, 1285) * mm, "end": v(4700, 1285) * mm});
            skLineSegment(sketch, "E192", {"start": v(4700, 1285) * mm, "end": v(4700, 200) * mm});
            skLineSegment(sketch, "E193", {"start": v(4700, 200) * mm, "end": v(4550, 200) * mm});
            skSolve(sketch);
        }
        {
            var Q0;
            Q0=makeQuery(id+"F38.imprint","IMPRINT",FACE,{"disambiguationData":[TD([[makeQuery(id+"F38.imprint","IMPRINT",EDGE,{"derivedFrom":sQuery(id+"F38.wireOp",EDGE,"E190")}),-1.0]])]});
            extrude(context, id + "F39", {"entities" : qUnion([Q0]), "operationType" : NewBodyOperationType.ADD, "depth" : 2400 * mm, "offsetDistance" : 25 * mm});
        }
        {
            var Q0;
            Q0=qCreatedBy(makeId("Top.planeOp"),FACE);
            var sketch = newSketch(context, id + "F40", { "sketchPlane" : qUnion([Q0])});
            skLineSegment(sketch, "E194.0", {"start": v(4700, 1285) * mm, "end": v(4700, 200) * mm});
            skLineSegment(sketch, "E194.1", {"start": v(7400, 200) * mm, "end": v(200, 200) * mm});
            skLineSegment(sketch, "E195", {"start": v(7400, 1285) * mm, "end": v(5590, 1285) * mm});
            skLineSegment(sketch, "E196", {"start": v(5590, 1285) * mm, "end": v(5590, 1210) * mm});
            skLineSegment(sketch, "E197", {"start": v(5590, 1210) * mm, "end": v(7400, 1210) * mm});
            skLineSegment(sketch, "E198", {"start": v(7400, 1210) * mm, "end": v(7400, 1285) * mm});
            skSolve(sketch);
        }
        {
            var Q0;
            Q0=makeQuery(id+"F40.imprint","IMPRINT",FACE,{"disambiguationData":[TD([[makeQuery(id+"F40.imprint","IMPRINT",EDGE,{"derivedFrom":sQuery(id+"F40.wireOp",EDGE,"E195")}),1.0]])]});
            extrude(context, id + "F41", {"entities" : qUnion([Q0]), "operationType" : NewBodyOperationType.ADD, "depth" : 2400 * mm, "offsetDistance" : 25 * mm});
        }
        {
            var Q0;
            Q0=qCreatedBy(makeId("Top.planeOp"),FACE);
            var sketch = newSketch(context, id + "F42", { "sketchPlane" : qUnion([Q0])});
            skLineSegment(sketch, "E199.0", {"start": v(7400, 1285) * mm, "end": v(5590, 1285) * mm});
            skLineSegment(sketch, "E199.1", {"start": v(7400, 5800) * mm, "end": v(7400, 200) * mm});
            skLineSegment(sketch, "E200", {"start": v(7400, 2225) * mm, "end": v(5590, 2225) * mm});
            skLineSegment(sketch, "E201", {"start": v(5590, 2225) * mm, "end": v(5590, 2300) * mm});
            skLineSegment(sketch, "E202", {"start": v(5590, 2300) * mm, "end": v(7400, 2300) * mm});
            skLineSegment(sketch, "E203", {"start": v(7400, 2300) * mm, "end": v(7400, 2225) * mm});
            skLineSegment(sketch, "E204", {"start": v(7400, 3240) * mm, "end": v(5590, 3240) * mm});
            skLineSegment(sketch, "E205", {"start": v(5590, 3240) * mm, "end": v(5590, 3315) * mm});
            skLineSegment(sketch, "E206", {"start": v(5590, 3315) * mm, "end": v(7400, 3315) * mm});
            skLineSegment(sketch, "E207", {"start": v(7400, 3315) * mm, "end": v(7400, 3240) * mm});
            skSolve(sketch);
        }
        {
            var Q0;
            Q0 = qSketchRegion(id + "F42", true);
            extrude(context, id + "F43", {"entities" : qUnion([Q0]), "operationType" : NewBodyOperationType.ADD, "depth" : 2400 * mm, "offsetDistance" : 25 * mm});
        }
        {
            var Q0;
            Q0=qCreatedBy(makeId("Top.planeOp"),FACE);
            var sketch = newSketch(context, id + "F44", { "sketchPlane" : qUnion([Q0])});
            skLineSegment(sketch, "E208.0", {"start": v(16170, 200) * mm, "end": v(8970, 200) * mm});
            skLineSegment(sketch, "E208.1", {"start": v(16170, 2940) * mm, "end": v(16170, 200) * mm});
            skLineSegment(sketch, "E209", {"start": v(14770, 200) * mm, "end": v(14770, 1110) * mm});
            skLineSegment(sketch, "E210", {"start": v(14770, 1110) * mm, "end": v(15120, 1110) * mm});
            skLineSegment(sketch, "E211", {"start": v(15120, 1110) * mm, "end": v(15120, 1260) * mm});
            skLineSegment(sketch, "E212", {"start": v(15120, 1260) * mm, "end": v(14620, 1260) * mm});
            skLineSegment(sketch, "E213", {"start": v(14620, 1260) * mm, "end": v(14620, 200) * mm});
            skLineSegment(sketch, "E214", {"start": v(14620, 200) * mm, "end": v(14770, 200) * mm});
            skSolve(sketch);
        }
        {
            var Q0;
            Q0 = qSketchRegion(id + "F44", true);
            extrude(context, id + "F45", {"entities" : qUnion([Q0]), "operationType" : NewBodyOperationType.ADD, "depth" : 2400 * mm, "offsetDistance" : 25 * mm});
        }
        {
            var Q0;
            Q0=qCreatedBy(makeId("Top.planeOp"),FACE);
            var sketch = newSketch(context, id + "F46", { "sketchPlane" : qUnion([Q0])});
            skLineSegment(sketch, "E215.0", {"start": v(1090, 2480) * mm, "end": v(1090, 5500) * mm});
            skLineSegment(sketch, "E216", {"start": v(1090, 5500) * mm, "end": v(0, 5500) * mm});
            skLineSegment(sketch, "E217", {"start": v(0, 5500) * mm, "end": v(0, 5300) * mm});
            skLineSegment(sketch, "E218", {"start": v(0, 5300) * mm, "end": v(1090, 5300) * mm});
            skLineSegment(sketch, "E219", {"start": v(1090, 5300) * mm, "end": v(1090, 5500) * mm});
            skSolve(sketch);
        }
        {
            var Q0;
            Q0 = qSketchRegion(id + "F46", true);
            extrude(context, id + "F47", {"entities" : qUnion([Q0]), "operationType" : NewBodyOperationType.ADD, "depth" : 2800 * mm, "offsetDistance" : 25 * mm});
        }
    });
